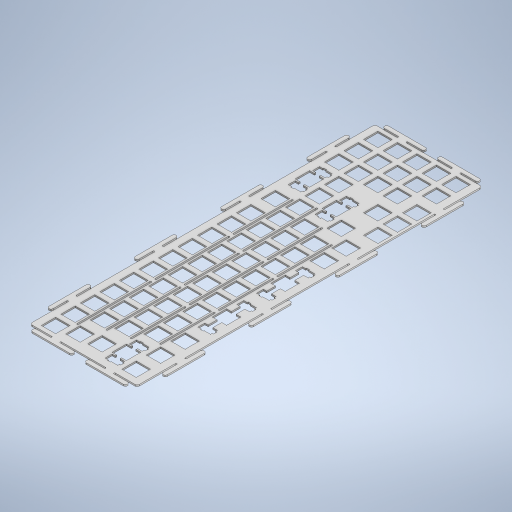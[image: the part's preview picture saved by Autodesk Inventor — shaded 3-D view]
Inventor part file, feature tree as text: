
AUTODESK INVENTOR PART (.ipt)
format: ipt  version: 2024 (Build 280153000, 153)  size: 1,393,664 bytes
history: native  units: mm
features: extrude x1, fillet x1, sketch x1
ambient origin geometry x8: Origin, YZ Plane, XZ Plane, XY Plane, X Axis, Y Axis, Z Axis, Center Point
bodies: 实体1 (feature_tree)
feature tree (3):
  extrude  "拉伸1"  Depth=7.0mm
  fillet  "圆角1"  Radius=4.0mm
  sketch  "草图1"  dims[d0=1.5mm d1=0.0mm d2=6.0mm d7=135.0deg d9=2.5mm d10=60.0deg d12=60.0deg d13=60.0deg d14=2.5mm d27=7.0mm d28=4.0mm d29=4.0mm d30=4.0mm d31=40.0mm d32=1.5mm d34=8.0mm d35=1.5mm d36=0.75mm d37=1.5mm d38=7.0mm d39=0.75mm d40=2.0mm d105=30.0497mm d114=42.0mm d115=42.0mm d116=84.0mm d117=84.0mm d118=4.0mm d119=40.0mm d120=8.0mm d121=0.75mm d122=0.75mm d123=2.0mm d124=4.0mm d125=40.0mm d126=8.0mm d127=0.75mm d128=0.75mm d129=2.0mm d130=4.0mm d131=40.0mm d132=8.0mm d133=0.75mm d134=0.75mm d135=2.0mm d142=4.0mm d143=40.0mm d144=8.0mm d145=0.75mm d146=0.75mm d147=2.0mm d148=4.0mm d149=40.0mm d150=8.0mm d151=0.75mm d152=0.75mm d153=2.0mm d154=4.0mm d155=40.0mm d156=8.0mm d157=0.75mm d158=0.75mm d159=2.0mm d160=4.0mm d161=40.0mm d162=8.0mm d163=0.75mm d164=0.75mm d165=2.0mm d166=26.0mm d167=26.0mm d168=4.0mm d169=40.0mm d170=8.0mm d171=0.75mm d172=0.75mm d173=2.0mm d174=4.0mm d175=40.0mm d176=8.0mm d177=0.75mm d178=0.75mm d179=2.0mm d186=4.0mm d187=40.0mm d188=8.0mm d189=0.75mm d190=0.75mm d191=2.0mm d192=4.0mm d193=40.0mm d194=8.0mm d195=0.75mm d196=0.75mm d197=2.0mm d198=2.0mm]
